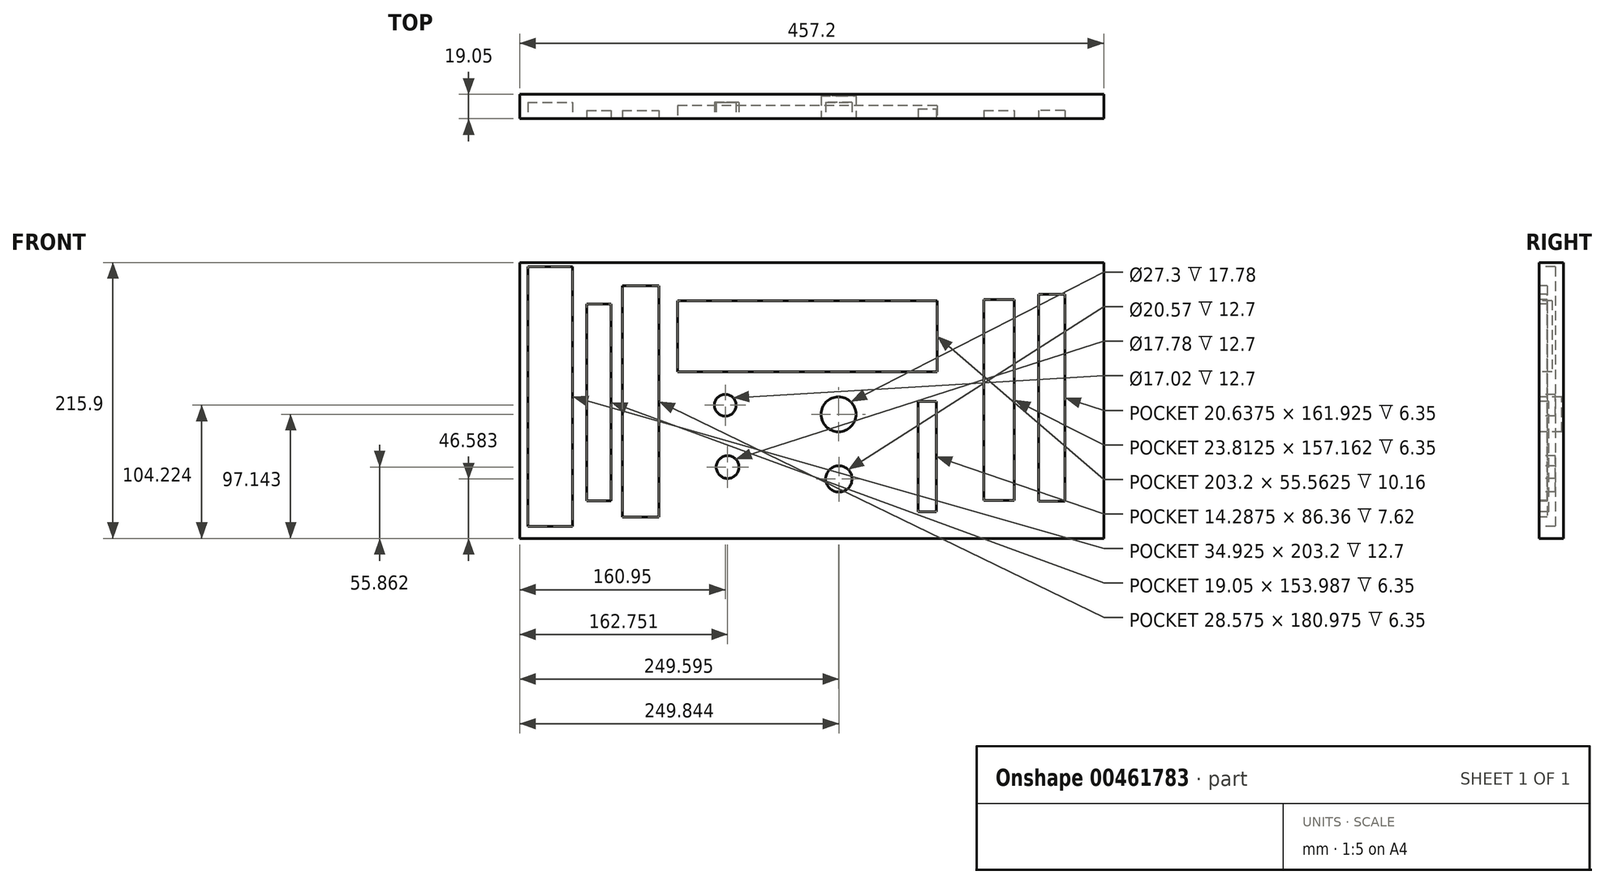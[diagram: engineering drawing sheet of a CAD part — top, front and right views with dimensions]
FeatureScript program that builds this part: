
annotation { "Feature Type Name" : "Feature", "Feature Type Description" : "" }
export const myFeature = defineFeature(function(context is Context, id is Id, definition is map)
    precondition{}
    {
        {
            var Q0;
            Q0=qCreatedBy(makeId("Front.planeOp"),FACE);
            var sketch = newSketch(context, id + "F0", { "sketchPlane" : qUnion([Q0])});
            skLineSegment(sketch, "E0", {"start": v(0, 0) * mm, "end": v(0, 215.9) * mm});
            skLineSegment(sketch, "E1", {"start": v(0, 215.9) * mm, "end": v(457.2, 215.9) * mm});
            skLineSegment(sketch, "E2", {"start": v(457.2, 215.9) * mm, "end": v(457.2, 0) * mm});
            skLineSegment(sketch, "E3", {"start": v(457.2, 0) * mm, "end": v(0, 0) * mm});
            skSolve(sketch);
        }
        {
            var Q0;
            Q0=makeQuery(id+"F0.imprint","IMPRINT",FACE,{"disambiguationData":[TD([[makeQuery(id+"F0.imprint","IMPRINT",EDGE,{"derivedFrom":sQuery(id+"F0.wireOp",EDGE,"E0")}),-1.0]])]});
            extrude(context, id + "F1", {"entities" : qUnion([Q0]), "oppositeDirection" : true, "depth" : 19.05 * mm});
        }
        {
            var Q0;
            Q0=qCreatedBy(makeId("Front.planeOp"),FACE);
            var sketch = newSketch(context, id + "F2", { "sketchPlane" : qUnion([Q0])});
            skLineSegment(sketch, "E4.bottom", {"start": v(426.7, 29) * mm, "end": v(406.07, 29) * mm});
            skLineSegment(sketch, "E4.top", {"start": v(426.7, 190.92) * mm, "end": v(406.07, 190.92) * mm});
            skLineSegment(sketch, "E4.left", {"start": v(426.7, 29) * mm, "end": v(426.7, 190.92) * mm});
            skLineSegment(sketch, "E4.right", {"start": v(406.07, 29) * mm, "end": v(406.07, 190.92) * mm});
            skSolve(sketch);
        }
        {
            var Q0;
            Q0=makeQuery(id+"F2.imprint","IMPRINT",FACE,{"disambiguationData":[TD([[makeQuery(id+"F2.imprint","IMPRINT",EDGE,{"derivedFrom":sQuery(id+"F2.wireOp",EDGE,"E4.bottom")}),-1.0]])]});
            extrude(context, id + "F3", {"entities" : qUnion([Q0]), "operationType" : NewBodyOperationType.REMOVE, "oppositeDirection" : true, "depth" : 6.35 * mm});
        }
        {
            var Q0;
            Q0=makeQuery(id+"F1.opExtrude","CAP_FACE",FACE,{"disambiguationData":[OSD([sQuery(id+"F0.wireOp",EDGE,"E0"),sQuery(id+"F0.wireOp",EDGE,"E1"),sQuery(id+"F0.wireOp",EDGE,"E2"),sQuery(id+"F0.wireOp",EDGE,"E3")])],"isStart":true});
            var sketch = newSketch(context, id + "F4", { "sketchPlane" : qUnion([Q0])});
            skLineSegment(sketch, "E5.bottom", {"start": v(363.38, 29.89) * mm, "end": v(387.19, 29.89) * mm});
            skLineSegment(sketch, "E5.top", {"start": v(363.38, 187.05) * mm, "end": v(387.19, 187.05) * mm});
            skLineSegment(sketch, "E5.left", {"start": v(363.38, 29.89) * mm, "end": v(363.38, 187.05) * mm});
            skLineSegment(sketch, "E5.right", {"start": v(387.19, 29.89) * mm, "end": v(387.19, 187.05) * mm});
            skSolve(sketch);
        }
        {
            var Q0;
            Q0=makeQuery(id+"F4.imprint","IMPRINT",FACE,{"disambiguationData":[TD([[makeQuery(id+"F4.imprint","IMPRINT",EDGE,{"derivedFrom":sQuery(id+"F4.wireOp",EDGE,"E5.bottom")}),1.0]])]});
            extrude(context, id + "F5", {"entities" : qUnion([Q0]), "operationType" : NewBodyOperationType.REMOVE, "oppositeDirection" : true, "depth" : 6.35 * mm});
        }
        {
            var Q0;
            Q0=makeQuery(id+"F1.opExtrude","CAP_FACE",FACE,{"disambiguationData":[OSD([sQuery(id+"F0.wireOp",EDGE,"E0"),sQuery(id+"F0.wireOp",EDGE,"E1"),sQuery(id+"F0.wireOp",EDGE,"E2"),sQuery(id+"F0.wireOp",EDGE,"E3")])],"isStart":true});
            var sketch = newSketch(context, id + "F6", { "sketchPlane" : qUnion([Q0])});
            skLineSegment(sketch, "E6.bottom", {"start": v(326.66, 186.03) * mm, "end": v(123.46, 186.03) * mm});
            skLineSegment(sketch, "E6.top", {"start": v(326.66, 130.47) * mm, "end": v(123.46, 130.47) * mm});
            skLineSegment(sketch, "E6.left", {"start": v(326.66, 186.03) * mm, "end": v(326.66, 130.47) * mm});
            skLineSegment(sketch, "E6.right", {"start": v(123.46, 186.03) * mm, "end": v(123.46, 130.47) * mm});
            skSolve(sketch);
        }
        {
            var Q0;
            Q0=makeQuery(id+"F6.imprint","IMPRINT",FACE,{"disambiguationData":[TD([[makeQuery(id+"F6.imprint","IMPRINT",EDGE,{"derivedFrom":sQuery(id+"F6.wireOp",EDGE,"E6.bottom")}),1.0]])]});
            extrude(context, id + "F7", {"entities" : qUnion([Q0]), "operationType" : NewBodyOperationType.REMOVE, "oppositeDirection" : true, "depth" : 10.16 * mm});
        }
        {
            var Q0;
            Q0=makeQuery(id+"F1.opExtrude","CAP_FACE",FACE,{"disambiguationData":[OSD([sQuery(id+"F0.wireOp",EDGE,"E0"),sQuery(id+"F0.wireOp",EDGE,"E1"),sQuery(id+"F0.wireOp",EDGE,"E2"),sQuery(id+"F0.wireOp",EDGE,"E3")])],"isStart":true});
            var sketch = newSketch(context, id + "F8", { "sketchPlane" : qUnion([Q0])});
            skLineSegment(sketch, "E7.bottom", {"start": v(311.73, 20.97) * mm, "end": v(326.02, 20.97) * mm});
            skLineSegment(sketch, "E7.top", {"start": v(311.73, 107.33) * mm, "end": v(326.02, 107.33) * mm});
            skLineSegment(sketch, "E7.left", {"start": v(311.73, 20.97) * mm, "end": v(311.73, 107.33) * mm});
            skLineSegment(sketch, "E7.right", {"start": v(326.02, 20.97) * mm, "end": v(326.02, 107.33) * mm});
            skSolve(sketch);
        }
        {
            var Q0;
            Q0=makeQuery(id+"F8.imprint","IMPRINT",FACE,{"disambiguationData":[TD([[makeQuery(id+"F8.imprint","IMPRINT",EDGE,{"derivedFrom":sQuery(id+"F8.wireOp",EDGE,"E7.bottom")}),1.0]])]});
            extrude(context, id + "F9", {"entities" : qUnion([Q0]), "operationType" : NewBodyOperationType.REMOVE, "oppositeDirection" : true, "depth" : 7.62 * mm});
        }
        {
            var Q0;
            Q0=makeQuery(id+"F1.opExtrude","CAP_FACE",FACE,{"disambiguationData":[OSD([sQuery(id+"F0.wireOp",EDGE,"E0"),sQuery(id+"F0.wireOp",EDGE,"E1"),sQuery(id+"F0.wireOp",EDGE,"E2"),sQuery(id+"F0.wireOp",EDGE,"E3")])],"isStart":true});
            var sketch = newSketch(context, id + "F10", { "sketchPlane" : qUnion([Q0])});
            skLineSegment(sketch, "E8.bottom", {"start": v(6.35, 212.65) * mm, "end": v(41.27, 212.65) * mm});
            skLineSegment(sketch, "E8.top", {"start": v(6.35, 9.45) * mm, "end": v(41.27, 9.45) * mm});
            skLineSegment(sketch, "E8.left", {"start": v(6.35, 212.65) * mm, "end": v(6.35, 9.45) * mm});
            skLineSegment(sketch, "E8.right", {"start": v(41.27, 212.65) * mm, "end": v(41.27, 9.45) * mm});
            skSolve(sketch);
        }
        {
            var Q0;
            Q0=makeQuery(id+"F10.imprint","IMPRINT",FACE,{"disambiguationData":[TD([[makeQuery(id+"F10.imprint","IMPRINT",EDGE,{"derivedFrom":sQuery(id+"F10.wireOp",EDGE,"E8.bottom")}),-1.0]])]});
            extrude(context, id + "F11", {"entities" : qUnion([Q0]), "operationType" : NewBodyOperationType.REMOVE, "oppositeDirection" : true, "depth" : 12.7 * mm});
        }
        {
            var Q0;
            Q0=makeQuery(id+"F1.opExtrude","CAP_FACE",FACE,{"disambiguationData":[OSD([sQuery(id+"F0.wireOp",EDGE,"E0"),sQuery(id+"F0.wireOp",EDGE,"E1"),sQuery(id+"F0.wireOp",EDGE,"E2"),sQuery(id+"F0.wireOp",EDGE,"E3")])],"isStart":true});
            var sketch = newSketch(context, id + "F12", { "sketchPlane" : qUnion([Q0])});
            skLineSegment(sketch, "E9.bottom", {"start": v(52.5, 183.47) * mm, "end": v(71.54, 183.47) * mm});
            skLineSegment(sketch, "E9.top", {"start": v(52.5, 29.48) * mm, "end": v(71.54, 29.48) * mm});
            skLineSegment(sketch, "E9.left", {"start": v(52.5, 183.47) * mm, "end": v(52.5, 29.48) * mm});
            skLineSegment(sketch, "E9.right", {"start": v(71.54, 183.47) * mm, "end": v(71.54, 29.48) * mm});
            skSolve(sketch);
        }
        {
            var Q0;
            Q0=makeQuery(id+"F12.imprint","IMPRINT",FACE,{"disambiguationData":[TD([[makeQuery(id+"F12.imprint","IMPRINT",EDGE,{"derivedFrom":sQuery(id+"F12.wireOp",EDGE,"E9.bottom")}),-1.0]])]});
            extrude(context, id + "F13", {"entities" : qUnion([Q0]), "operationType" : NewBodyOperationType.REMOVE, "oppositeDirection" : true, "depth" : 6.35 * mm});
        }
        {
            var Q0;
            Q0=makeQuery(id+"F1.opExtrude","CAP_FACE",FACE,{"disambiguationData":[OSD([sQuery(id+"F0.wireOp",EDGE,"E0"),sQuery(id+"F0.wireOp",EDGE,"E1"),sQuery(id+"F0.wireOp",EDGE,"E2"),sQuery(id+"F0.wireOp",EDGE,"E3")])],"isStart":true});
            var sketch = newSketch(context, id + "F14", { "sketchPlane" : qUnion([Q0])});
            skCircle(sketch, "E10", {"center": v(249.6, 97.14) * mm, "radius": 13.65 * mm});
            skSolve(sketch);
        }
        {
            var Q0;
            Q0=makeQuery(id+"F14.imprint","IMPRINT",FACE,{"disambiguationData":[TD([[makeQuery(id+"F14.imprint","IMPRINT",EDGE,{"derivedFrom":sQuery(id+"F14.wireOp",EDGE,"E10")}),1.0]])]});
            extrude(context, id + "F15", {"entities" : qUnion([Q0]), "operationType" : NewBodyOperationType.REMOVE, "oppositeDirection" : true, "depth" : 17.78 * mm});
        }
        {
            var Q0;
            Q0=makeQuery(id+"F1.opExtrude","CAP_FACE",FACE,{"disambiguationData":[OSD([sQuery(id+"F0.wireOp",EDGE,"E0"),sQuery(id+"F0.wireOp",EDGE,"E1"),sQuery(id+"F0.wireOp",EDGE,"E2"),sQuery(id+"F0.wireOp",EDGE,"E3")])],"isStart":true});
            var sketch = newSketch(context, id + "F16", { "sketchPlane" : qUnion([Q0])});
            skCircle(sketch, "E11", {"center": v(249.84, 46.58) * mm, "radius": 10.29 * mm});
            skSolve(sketch);
        }
        {
            var Q0;
            Q0=makeQuery(id+"F16.imprint","IMPRINT",FACE,{"disambiguationData":[TD([[makeQuery(id+"F16.imprint","IMPRINT",EDGE,{"derivedFrom":sQuery(id+"F16.wireOp",EDGE,"E11")}),1.0]])]});
            extrude(context, id + "F17", {"entities" : qUnion([Q0]), "operationType" : NewBodyOperationType.REMOVE, "oppositeDirection" : true, "depth" : 12.7 * mm});
        }
        {
            var Q0;
            Q0=makeQuery(id+"F1.opExtrude","CAP_FACE",FACE,{"disambiguationData":[OSD([sQuery(id+"F0.wireOp",EDGE,"E0"),sQuery(id+"F0.wireOp",EDGE,"E1"),sQuery(id+"F0.wireOp",EDGE,"E2"),sQuery(id+"F0.wireOp",EDGE,"E3")])],"isStart":true});
            var sketch = newSketch(context, id + "F18", { "sketchPlane" : qUnion([Q0])});
            skCircle(sketch, "E12", {"center": v(162.75, 55.86) * mm, "radius": 8.9 * mm});
            skSolve(sketch);
        }
        {
            var Q0;
            Q0=makeQuery(id+"F18.imprint","IMPRINT",FACE,{"disambiguationData":[TD([[makeQuery(id+"F18.imprint","IMPRINT",EDGE,{"derivedFrom":sQuery(id+"F18.wireOp",EDGE,"E12")}),1.0]])]});
            extrude(context, id + "F19", {"entities" : qUnion([Q0]), "operationType" : NewBodyOperationType.REMOVE, "oppositeDirection" : true, "depth" : 12.7 * mm});
        }
        {
            var Q0;
            Q0=makeQuery(id+"F1.opExtrude","CAP_FACE",FACE,{"disambiguationData":[OSD([sQuery(id+"F0.wireOp",EDGE,"E0"),sQuery(id+"F0.wireOp",EDGE,"E1"),sQuery(id+"F0.wireOp",EDGE,"E2"),sQuery(id+"F0.wireOp",EDGE,"E3")])],"isStart":true});
            var sketch = newSketch(context, id + "F20", { "sketchPlane" : qUnion([Q0])});
            skCircle(sketch, "E13", {"center": v(160.95, 104.22) * mm, "radius": 8.5 * mm});
            skSolve(sketch);
        }
        {
            var Q0;
            Q0=makeQuery(id+"F20.imprint","IMPRINT",FACE,{"disambiguationData":[TD([[makeQuery(id+"F20.imprint","IMPRINT",EDGE,{"derivedFrom":sQuery(id+"F20.wireOp",EDGE,"E13")}),1.0]])]});
            extrude(context, id + "F21", {"entities" : qUnion([Q0]), "operationType" : NewBodyOperationType.REMOVE, "oppositeDirection" : true, "depth" : 12.7 * mm});
        }
        {
            var Q0;
            Q0=makeQuery(id+"F1.opExtrude","CAP_FACE",FACE,{"disambiguationData":[OSD([sQuery(id+"F0.wireOp",EDGE,"E0"),sQuery(id+"F0.wireOp",EDGE,"E1"),sQuery(id+"F0.wireOp",EDGE,"E2"),sQuery(id+"F0.wireOp",EDGE,"E3")])],"isStart":true});
            var sketch = newSketch(context, id + "F22", { "sketchPlane" : qUnion([Q0])});
            skLineSegment(sketch, "E14.bottom", {"start": v(80.31, 197.87) * mm, "end": v(108.89, 197.87) * mm});
            skLineSegment(sketch, "E14.top", {"start": v(80.31, 16.9) * mm, "end": v(108.89, 16.9) * mm});
            skLineSegment(sketch, "E14.left", {"start": v(80.31, 197.87) * mm, "end": v(80.31, 16.9) * mm});
            skLineSegment(sketch, "E14.right", {"start": v(108.89, 197.87) * mm, "end": v(108.89, 16.9) * mm});
            skSolve(sketch);
        }
        {
            var Q0;
            Q0=makeQuery(id+"F22.imprint","IMPRINT",FACE,{"disambiguationData":[TD([[makeQuery(id+"F22.imprint","IMPRINT",EDGE,{"derivedFrom":sQuery(id+"F22.wireOp",EDGE,"E14.bottom")}),-1.0]])]});
            extrude(context, id + "F23", {"entities" : qUnion([Q0]), "operationType" : NewBodyOperationType.REMOVE, "oppositeDirection" : true, "depth" : 6.35 * mm});
        }
    });
